FCSTD DOCUMENT  (FreeCAD 0.21R33675 (Git))
Label: Rotor_Front
License: All rights reserved
LicenseURL: http://en.wikipedia.org/wiki/All_rights_reserved
objects: App::Link×2, Spreadsheet::Sheet×1, App::Part×1
EXTERNAL_REF file=Rotor_Disk_Front.FCStd obj=Body
EXTERNAL_REF file=../../Master_of_Puppets.FCStd obj=Alternator
EXTERNAL_REF file=../../Master_of_Puppets.FCStd obj=Spreadsheet
EXTERNAL_REF file=Rotor_Disk_Front_ReducedWeight.FCStd obj=Body001
EXTERNAL_REF file=MagnetResin_Assembly.FCStd obj=Part

FEATURE [App::Link] Link  label="Rotor_Disk"
  LinkPlacement = pos=(3.6e-15,0,0) rot=(0,0,1;0rad)
  LinkedObject = -> <external Rotor_Disk_Front.FCStd>#Body
  Placement = pos=(3.6e-15,0,0) rot=(0,0,1;0rad)
  expr: LinkedObject = Spreadsheet.Disk
FEATURE [Spreadsheet::Sheet] Spreadsheet
  cells = A1='Inputs; A2='RotorDiskRadius; B2(RotorDiskRadius)==Master_of_Puppets#Spreadsheet.RotorDiskRadius; A3='WeightReductionRotorDiskRadiusThreshold; B3(WeightReductionRotorDiskRadiusThreshold)==Master_of_Puppets#Alternator.WeightReductionRotorDiskRadiusThreshold; A4='Disk; A5='DiskFullWeight; B5(DiskFullWeight)==<<Rotor_Disk_Front>>#<<Rotor_Disk_Front>>._self; A6='DiskReducedWeight; B6(DiskReducedWeight)==<<Rotor_Disk_Front_ReducedWeight>>#<<Rotor_Disk_Front>>._self; A7='Disk; B7(Disk)==RotorDiskRadius <= WeightReductionRotorDiskRadiusThreshold ? DiskFullWeight : DiskReducedWeight
FEATURE [App::Link] Link003  label="MagnetResin_Assembly"
  LinkedObject = -> <external MagnetResin_Assembly.FCStd>#Part
FEATURE [App::Part] Part  label="Rotor"
  Group = -> [Link,Link003]
  Origin = -> Origin
  Placement = pos=(0,0,0) rot=(0,1,0;3.14159rad)

RESOLVED EXTERNAL PARTS (link-assembly join: the EXTERNAL_REF files above that resolve inside this repo's crawl, each included once):
---- part ../../Master_of_Puppets.FCStd = doc fcstd_6404554055c4 (61625 chars; too large to inline — full recipe in that document) ----
---- part MagnetResin_Assembly.FCStd = doc fcstd_793aa970f8d2 ----
FCSTD DOCUMENT  (FreeCAD 0.19R24366 (Git))
Label: MagnetResin_Assembly
License: All rights reserved
LicenseURL: http://en.wikipedia.org/wiki/All_rights_reserved
objects: App::Link×2, App::Part×1, Spreadsheet::Sheet×1
EXTERNAL_REF file=Rotor_ResinCast.FCStd obj=PocketBody
EXTERNAL_REF file=Rotor_Magnets.FCStd obj=Array
EXTERNAL_REF file=../../Master_of_Puppets.FCStd obj=Spreadsheet

FEATURE [App::Link] Link001  label="Rotor_ResinCast"
  LinkPlacement = pos=(3.6e-15,0,0) rot=(0,0,1;0rad)
  LinkedObject = -> <external Rotor_ResinCast.FCStd>#PocketBody
  Placement = pos=(3.6e-15,0,0) rot=(0,0,1;0rad)
FEATURE [App::Link] Link002  label="Rotor_Magnets"
  LinkPlacement = pos=(3.6e-15,0,10) rot=(0,0,1;0rad)
  LinkedObject = -> <external Rotor_Magnets.FCStd>#Array
  Placement = pos=(3.6e-15,0,10) rot=(0,0,1;0rad)
  expr: .Placement.Base.z = Spreadsheet.MagnetAssemblyZ
FEATURE [App::Part] Part  label="MagnetResin_Assembly"
  Group = -> [Link001,Link002]
  Origin = -> Origin
  Placement = pos=(0,0,0) rot=(0,1,0;3.14159rad)
FEATURE [Spreadsheet::Sheet] Spreadsheet
  cells = A1=Inputs; A2=RotorDiskThickness; B2(RotorDiskThickness)==Master_of_Puppets#Spreadsheet.RotorDiskThickness; A3=Magnet Assembly; A4=MagnetAssemblyZ; B4(MagnetAssemblyZ)==RotorDiskThickness
---- part Rotor_Disk_Front.FCStd = doc fcstd_8f7620c75503 ----
FCSTD DOCUMENT  (FreeCAD 1.0R39109 (Git))
Label: Rotor_Disk_Front
License: All rights reserved
LicenseURL: http://en.wikipedia.org/wiki/All_rights_reserved
objects: Spreadsheet::Sheet×1, Sketcher::SketchObject×1, PartDesign::SubShapeBinder×1, PartDesign::FeatureBase×1, PartDesign::Pocket×1, PartDesign::PolarPattern×1, PartDesign::Body×1, App::Link×1
note: 11 computed .brp shape members not serialized (recipe doc carries the construction recipe); baked Part::Feature solids carry a one-line shape summary decoded from their .brp
EXTERNAL_REF file=../../Master_of_Puppets.FCStd obj=Alternator
EXTERNAL_REF file=../../Master_of_Puppets.FCStd obj=Hub
EXTERNAL_REF file=../../Master_of_Puppets.FCStd obj=Spreadsheet
EXTERNAL_REF file=Rotor_Disk_Back.FCStd obj=Pocket001Body

FEATURE [Spreadsheet::Sheet] Spreadsheet
  cells = A1='Inputs; A2='CalculatedWindTurbineShape; B2(CalculatedWindTurbineShape)==Master_of_Puppets#Spreadsheet.CalculatedWindTurbineShape; A3='HubPitchCircleRadius; B3(HubPitchCircleRadius)==Master_of_Puppets#Hub.HubPitchCircleRadius; A4='RotorDiskThickness; B4(RotorDiskThickness)==Master_of_Puppets#Spreadsheet.RotorDiskThickness; A5='HubHolesRadius; B5(HubHolesRadius)==Master_of_Puppets#Hub.HubHolesRadius; A6='NumberOfJackingHoles; B6(NumberOfJackingHoles)==Master_of_Puppets#Alternator.NumberOfJackingHoles; A7='JackingHoleDiameter; B7(JackingHoleDiameter)==Master_of_Puppets#Alternator.JackingHoleDiameter; A8='IslandRadius; B8(IslandRadius)==Master_of_Puppets#Alternator.IslandRadius; A9='Calculated; A10='JackingHoleRadius; B10(JackingHoleRadius)==JackingHoleDiameter / 2; A11='DistanceOfHolesFromCenter; A12='TShapeDistanceOfHolesFromCenter; B12(TShapeDistanceOfHolesFromCenter)==HubPitchCircleRadius; A13='HShapeDistanceOfHolesFromCenter; B13(HShapeDistanceOfHolesFromCenter)==(IslandRadius - HubPitchCircleRadius + HubHolesRadius) / 2 + HubPitchCircleRadius; A14='DistanceOfHolesFromCenter; B14(DistanceOfHolesFromCenter)==CalculatedWindTurbineShape == <<T>> ? TShapeDistanceOfHolesFromCenter : HShapeDistanceOfHolesFromCenter; A15='HoleAngle; A16='TShapeHoleAngle; B16(TShapeHoleAngle)==45 deg; A17='HShapeHoleAngle; B17(HShapeHoleAngle)==90 deg; A18='HoleAngle; B18(HoleAngle)==CalculatedWindTurbineShape == <<T>> ? TShapeHoleAngle : HShapeHoleAngle
FEATURE [Sketcher::SketchObject] Sketch
  ArcFitTolerance = 0
  AttachmentOffset = pos=(0,0,10) rot=(0,0,1;0rad)
  AttachmentSupport = -> [XY_Plane]
  FullyConstrained = true
  MakeInternals = false
  MapMode = 5
  Placement = pos=(0,0,10) rot=(0,0,1;0rad)
  expr: .AttachmentOffset.Base.z = Spreadsheet.RotorDiskThickness
  expr: Constraints[0] = Spreadsheet.JackingHoleRadius
  expr: Constraints[3] = Spreadsheet.HoleAngle
  expr: Constraints[4] = Spreadsheet.DistanceOfHolesFromCenter
  sketch-geometry (2):
    g0: Circle CenterX=35.3553 CenterY=35.3553 CenterZ=0 NormalX=0 NormalY=0 NormalZ=1 AngleXU=0 Radius=5.125
    g1: LineSegment [constr] StartX=35.3553 StartY=35.3553 StartZ=0 EndX=-6e-16 EndY=1e-15 EndZ=0
  constraints (5):
    c: Radius(g0) = 5.125
    c: Coincident(g1,g0)
    c: Coincident(g1,g-1)
    c: Angle(g-1,g1) = 0.785398
    c: Distance(g-1,g0) = 50
FEATURE [PartDesign::SubShapeBinder] Binder
  BindCopyOnChange = 0
  BindMode = 0
  ClaimChildren = false
  Context = -> Body [Binder.]
  Fuse = false
  MakeFace = true
  OffsetFill = false
  OffsetIntersection = false
  OffsetJoinType = 0
  OffsetOpenResult = false
  PartialLoad = false
  Refine = true
  Relative = true
  Support = -> [Link]
  _Version = 2
FEATURE [PartDesign::FeatureBase] BaseFeature
  BaseFeature = -> Binder
  Suppressed = false
FEATURE [PartDesign::Pocket] Pocket
  BaseFeature = -> BaseFeature
  Direction = (0,0,-1)
  Length = 5
  Length2 = 100
  Profile = -> Sketch
  Suppressed = false
  Type = 1
FEATURE [PartDesign::PolarPattern] PolarPattern
  Angle = 360
  Axis = -> Sketch [N_Axis]
  BaseFeature = -> Pocket
  Mode = 0
  Occurrences = 4
  Offset = 120
  Originals = -> [Pocket]
  Suppressed = false
  TransformMode = 0
  expr: Occurrences = Spreadsheet.NumberOfJackingHoles
FEATURE [PartDesign::Body] Body  label="Rotor_Disk_Front"
  AllowCompound = false
  BaseFeature = -> Binder
  Group = -> [BaseFeature,Binder,Sketch,Pocket,PolarPattern]
  Openafpm_Flat = true
  Origin = -> Origin
  Tip = -> PolarPattern
FEATURE [App::Link] Link  label="Rotor_Disk_Back"
  LinkedObject = -> <external Rotor_Disk_Back.FCStd>#Pocket001Body
---- part Rotor_Disk_Front_ReducedWeight.FCStd = doc fcstd_32e151eb0e62 ----
FCSTD DOCUMENT  (FreeCAD 0.21R33771 (Git))
Label: Rotor_Disk_Front_ReducedWeight
License: All rights reserved
LicenseURL: http://en.wikipedia.org/wiki/All_rights_reserved
objects: Spreadsheet::Sheet×1, App::Link×1, PartDesign::SubShapeBinder×1, Sketcher::SketchObject×1, PartDesign::FeatureBase×1, PartDesign::Pocket×1, PartDesign::PolarPattern×1, PartDesign::Body×1
note: 7 computed .brp shape members not serialized (recipe doc carries the construction recipe); baked Part::Feature solids carry a one-line shape summary decoded from their .brp
EXTERNAL_REF file=../../Master_of_Puppets.FCStd obj=Alternator
EXTERNAL_REF file=Rotor_Disk_Back_ReducedWeight.FCStd obj=Body

FEATURE [Spreadsheet::Sheet] Spreadsheet
  cells = A1='Inputs; A2='Alternator; A3='NumberOfJackingHoles; B3(NumberOfJackingHoles)==Master_of_Puppets#Alternator.NumberOfJackingHoles; A4='JackingHoleDiameter; B4(JackingHoleDiameter)==Master_of_Puppets#Alternator.JackingHoleDiameter; A5='PocketInnerRadius; B5(PocketInnerRadius)==Master_of_Puppets#Alternator.PocketInnerRadius; A6='PocketOuterRadius; B6(PocketOuterRadius)==Master_of_Puppets#Alternator.PocketOuterRadius; A7='Calculated; A8='JackingHoleRadius; B8(JackingHoleRadius)==JackingHoleDiameter / 2; A9='RadiusSmallHoles; B9(RadiusSmallHoles)==(PocketOuterRadius - PocketInnerRadius) / 2 + PocketInnerRadius
FEATURE [App::Link] Link  label="Rotor_Disk_Back_ReducedWeight"
  LinkedObject = -> <external Rotor_Disk_Back_ReducedWeight.FCStd>#Body
FEATURE [PartDesign::SubShapeBinder] Binder
  BindCopyOnChange = 0
  BindMode = 0
  ClaimChildren = false
  Context = -> Body001 [Binder.]
  Fuse = false
  MakeFace = true
  OffsetFill = false
  OffsetIntersection = false
  OffsetJoinType = 0
  OffsetOpenResult = false
  PartialLoad = false
  Refine = true
  Relative = true
  Support = -> [Link]
  _Version = 2
FEATURE [Sketcher::SketchObject] Sketch003  label="JackingHoleSketch"
  FullyConstrained = true
  MapMode = 5
  Placement = pos=(0,0,0) rot=(1,0,0;3.14159rad)
  expr: Constraints[2] = Spreadsheet.RadiusSmallHoles
  expr: Constraints[3] = Spreadsheet.JackingHoleRadius
  sketch-geometry (2):
    g0: Circle CenterX=-33.75 CenterY=58.4567 CenterZ=0 NormalX=0 NormalY=0 NormalZ=1 AngleXU=0 Radius=5.125
    g1: LineSegment StartX=-33.75 StartY=58.4567 StartZ=0 EndX=0 EndY=0 EndZ=0
  constraints (5):
    c: Coincident(g1,g0)
    c: Coincident(g1,g-1)
    c: Distance(g1) = 67.5
    c: Radius(g0) = 5.125
    c: Angle(g-2,g1) = 0.523599
FEATURE [PartDesign::FeatureBase] BaseFeature001  label="BaseFeature"
  BaseFeature = -> Binder
FEATURE [PartDesign::Pocket] Pocket
  BaseFeature = -> BaseFeature001
  Direction = (0,0,1)
  Length = 5
  Length2 = 100
  Profile = -> Sketch003
  Type = 1
FEATURE [PartDesign::PolarPattern] PolarPattern
  Angle = 360
  Axis = -> Sketch003 [N_Axis]
  BaseFeature = -> Pocket
  Occurrences = 4
  Originals = -> [Pocket]
  expr: Occurrences = Spreadsheet.NumberOfJackingHoles
FEATURE [PartDesign::Body] Body001  label="Rotor_Disk_Front"
  BaseFeature = -> Binder
  Group = -> [BaseFeature001,Binder,Sketch003,Pocket,PolarPattern]
  Openafpm_Flat = true
  Origin = -> Origin001
  Tip = -> PolarPattern
